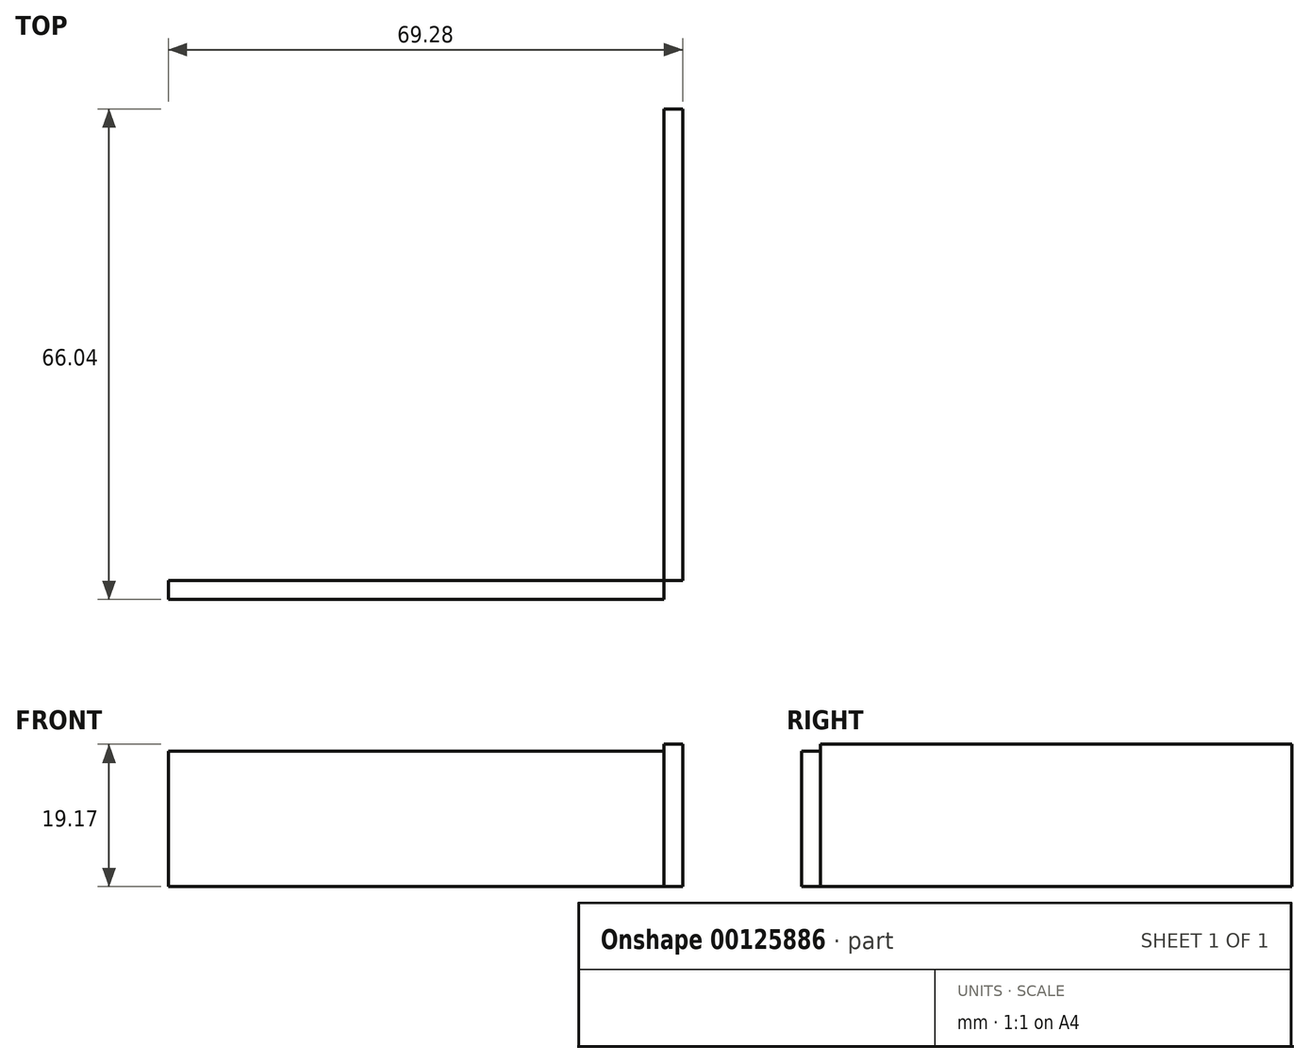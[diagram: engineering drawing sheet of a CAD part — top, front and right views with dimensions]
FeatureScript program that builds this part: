
annotation { "Feature Type Name" : "Feature", "Feature Type Description" : "" }
export const myFeature = defineFeature(function(context is Context, id is Id, definition is map)
    precondition{}
    {
        {
            var Q0;
            Q0=qCreatedBy(makeId("Front.planeOp"),FACE);
            var sketch = newSketch(context, id + "F0", { "sketchPlane" : qUnion([Q0])});
            skLineSegment(sketch, "E0.bottom", {"start": v(-66.74, 18.25) * mm, "end": v(0, 18.25) * mm});
            skLineSegment(sketch, "E0.top", {"start": v(-66.74, 0) * mm, "end": v(0, 0) * mm});
            skLineSegment(sketch, "E0.left", {"start": v(-66.74, 18.25) * mm, "end": v(-66.74, 0) * mm});
            skLineSegment(sketch, "E0.right", {"start": v(0, 18.25) * mm, "end": v(0, 0) * mm});
            skSolve(sketch);
        }
        {
            var Q0;
            Q0=qCreatedBy(makeId("Right.planeOp"),FACE);
            var sketch = newSketch(context, id + "F1", { "sketchPlane" : qUnion([Q0])});
            skLineSegment(sketch, "E1.bottom", {"start": v(0, 19.17) * mm, "end": v(63.5, 19.17) * mm});
            skLineSegment(sketch, "E1.top", {"start": v(0, 0) * mm, "end": v(63.5, 0) * mm});
            skLineSegment(sketch, "E1.left", {"start": v(0, 19.17) * mm, "end": v(0, 0) * mm});
            skLineSegment(sketch, "E1.right", {"start": v(63.5, 19.17) * mm, "end": v(63.5, 0) * mm});
            skSolve(sketch);
        }
        {
            var Q0;
            Q0=makeQuery(id+"F1.imprint","IMPRINT",FACE,{"disambiguationData":[TD([[makeQuery(id+"F1.imprint","IMPRINT",EDGE,{"derivedFrom":sQuery(id+"F1.wireOp",EDGE,"E1.bottom")}),-1.0]])]});
            extrude(context, id + "F2", {"entities" : qUnion([Q0]), "depth" : 2.54 * mm});
        }
        {
            var Q0;
            Q0 = qSketchRegion(id + "F0", true);
            extrude(context, id + "F3", {"entities" : qUnion([Q0]), "depth" : 2.54 * mm});
        }
    });
